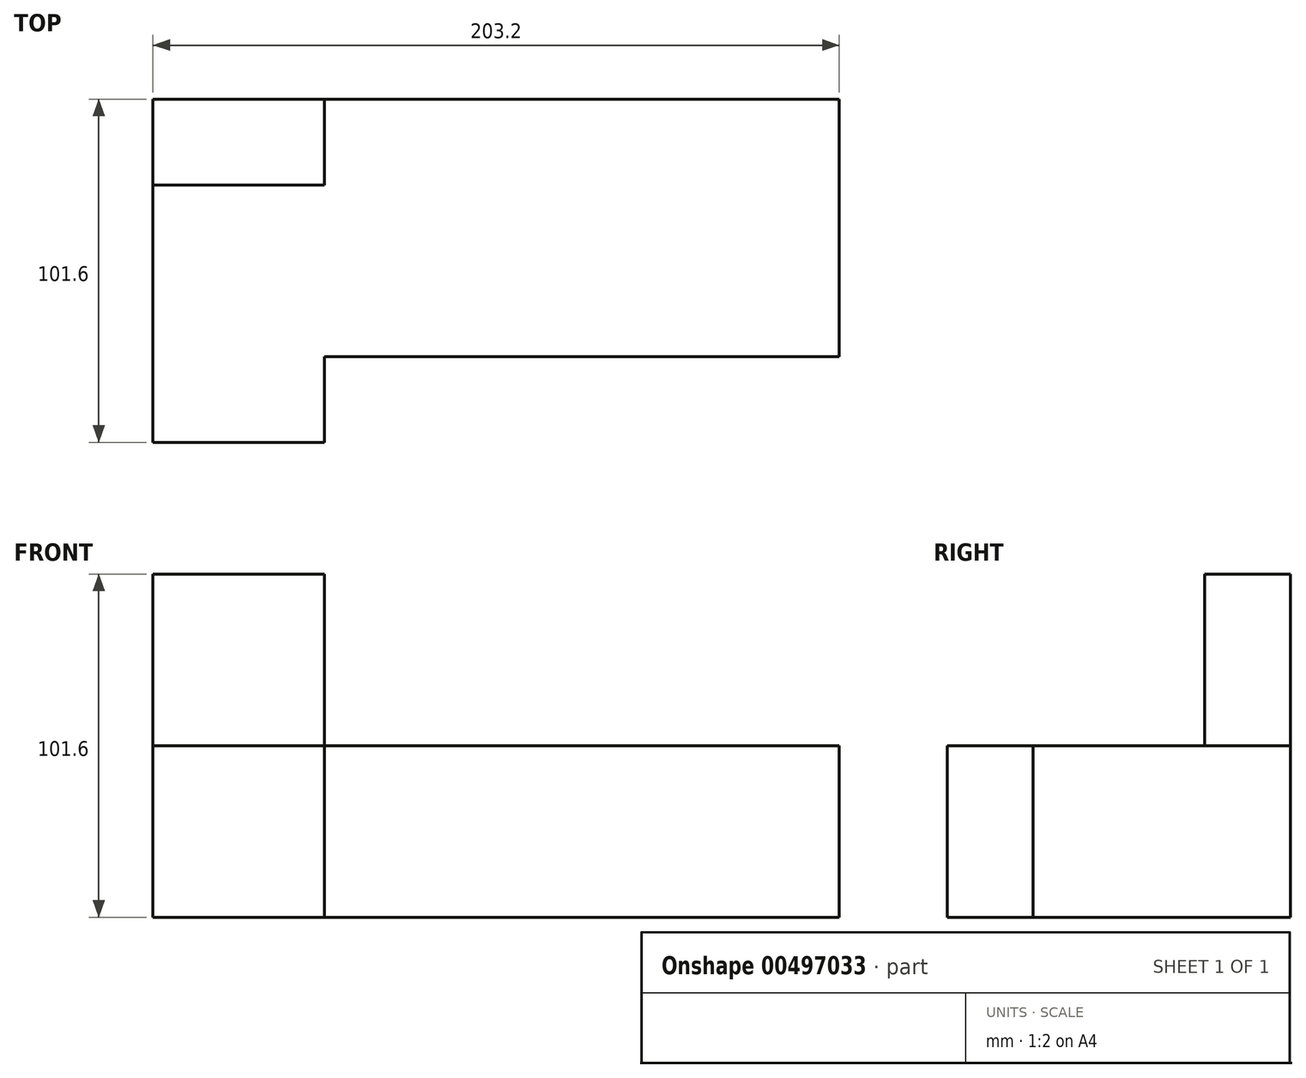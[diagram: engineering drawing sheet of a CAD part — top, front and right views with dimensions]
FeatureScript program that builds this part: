
annotation { "Feature Type Name" : "Feature", "Feature Type Description" : "" }
export const myFeature = defineFeature(function(context is Context, id is Id, definition is map)
    precondition{}
    {
        {
            var Q0;
            Q0=qCreatedBy(makeId("Front.planeOp"),FACE);
            var sketch = newSketch(context, id + "F0", { "sketchPlane" : qUnion([Q0])});
            skLineSegment(sketch, "E0.left", {"start": v(0, 0) * mm, "end": v(0, 50.8) * mm});
            skLineSegment(sketch, "E0.right", {"start": v(203.2, 0) * mm, "end": v(203.2, 50.8) * mm});
            skLineSegment(sketch, "E1.right", {"start": v(50.8, 0) * mm, "end": v(50.8, 50.8) * mm});
            skLineSegment(sketch, "E2", {"start": v(50.8, 50.8) * mm, "end": v(203.2, 50.8) * mm});
            skLineSegment(sketch, "E3", {"start": v(203.2, 0) * mm, "end": v(50.8, 0) * mm});
            skLineSegment(sketch, "E4", {"start": v(50.8, 0) * mm, "end": v(0, 0) * mm});
            skLineSegment(sketch, "E5", {"start": v(0, 50.8) * mm, "end": v(50.8, 50.8) * mm});
            skLineSegment(sketch, "E6.top", {"start": v(0, 101.6) * mm, "end": v(50.8, 101.6) * mm});
            skLineSegment(sketch, "E6.left", {"start": v(0, 50.8) * mm, "end": v(0, 101.6) * mm});
            skLineSegment(sketch, "E6.right", {"start": v(50.8, 50.8) * mm, "end": v(50.8, 101.6) * mm});
            skSolve(sketch);
        }
        {
            var Q0;
            Q0=makeQuery(id+"F0.imprint","IMPRINT",FACE,{"disambiguationData":[TD([[makeQuery(id+"F0.imprint","IMPRINT",EDGE,{"derivedFrom":sQuery(id+"F0.wireOp",EDGE,"E0.left")}),-1.0]])]});
            extrude(context, id + "F1", {"entities" : qUnion([Q0]), "depth" : 101.6 * mm});
        }
        {
            var Q0;
            Q0=makeQuery(id+"F0.imprint","IMPRINT",FACE,{"disambiguationData":[TD([[makeQuery(id+"F0.imprint","IMPRINT",EDGE,{"derivedFrom":sQuery(id+"F0.wireOp",EDGE,"E0.right")}),1.0]])]});
            extrude(context, id + "F2", {"entities" : qUnion([Q0]), "operationType" : NewBodyOperationType.ADD, "depth" : 76.2 * mm});
        }
        {
            var Q0;
            Q0=makeQuery(id+"F0.imprint","IMPRINT",FACE,{"disambiguationData":[TD([[makeQuery(id+"F0.imprint","IMPRINT",EDGE,{"derivedFrom":sQuery(id+"F0.wireOp",EDGE,"E5")}),1.0]])]});
            extrude(context, id + "F3", {"entities" : qUnion([Q0]), "operationType" : NewBodyOperationType.ADD, "depth" : 25.4 * mm});
        }
    });
